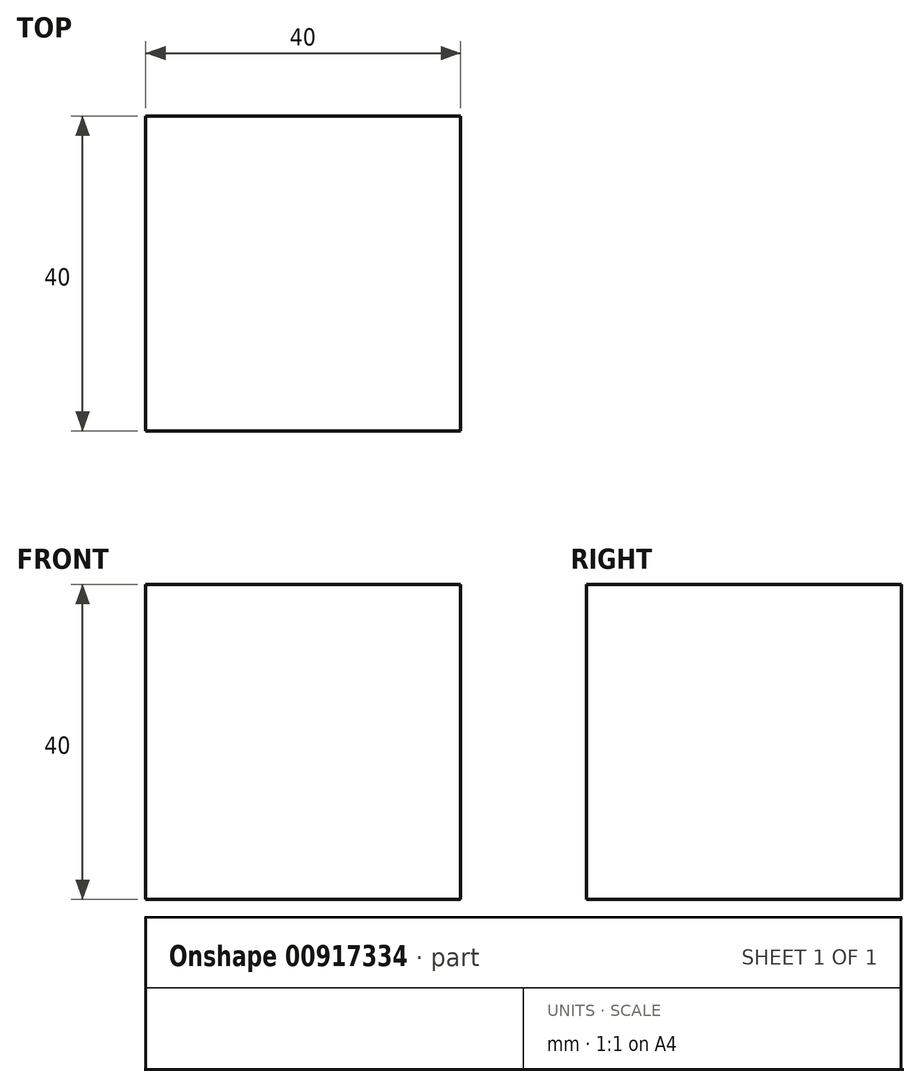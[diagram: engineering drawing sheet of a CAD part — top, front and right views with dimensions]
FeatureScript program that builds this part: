
annotation { "Feature Type Name" : "Feature", "Feature Type Description" : "" }
export const myFeature = defineFeature(function(context is Context, id is Id, definition is map)
    precondition{}
    {
        {
            var Q0;
            Q0=qCreatedBy(makeId("Top.planeOp"),FACE);
            var sketch = newSketch(context, id + "F0", { "sketchPlane" : qUnion([Q0])});
            skLineSegment(sketch, "E0.bottom", {"start": v(-19.67, 25.02) * mm, "end": v(20.33, 25.02) * mm});
            skLineSegment(sketch, "E0.top", {"start": v(-19.67, -14.98) * mm, "end": v(20.33, -14.98) * mm});
            skLineSegment(sketch, "E0.left", {"start": v(-19.67, 25.02) * mm, "end": v(-19.67, -14.98) * mm});
            skLineSegment(sketch, "E0.right", {"start": v(20.33, 25.02) * mm, "end": v(20.33, -14.98) * mm});
            skSolve(sketch);
        }
        {
            var Q0;
            Q0=makeQuery(id+"F0.imprint","IMPRINT",FACE,{"disambiguationData":[TD([[makeQuery(id+"F0.imprint","IMPRINT",EDGE,{"derivedFrom":sQuery(id+"F0.wireOp",EDGE,"E0.bottom")}),-1.0]])]});
            extrude(context, id + "F1", {"entities" : qUnion([Q0]), "depth" : 40 * mm, "offsetDistance" : 25 * mm});
        }
    });
